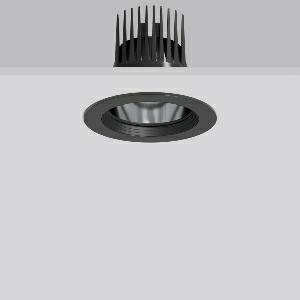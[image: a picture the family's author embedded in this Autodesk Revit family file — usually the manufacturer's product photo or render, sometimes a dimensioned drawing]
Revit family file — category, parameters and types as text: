
# Revit family: heledon_maxi_e_901765_003_2_6d95
name_source: partatom
category: Lighting Fixtures
units: mm (PartAtom-declared; Revit-internal decimal feet)

## family parameters
Cut with Voids When Loaded = No
Host = Face
Light Source = No
Part Type = Normal
Room Calculation Point = No
Round Connector Dimension = Use Diameter
Shared = No

## types (1)
- HELEDON maxi E (1 x LED Modul 927, 4100 lm, 2700)
    Apparent Load = 35 VA
    Approval mark = CE
    CIE Flux Codes = 100 100 100 100 100
    Color Rendering = 92
    Color Temperature = 2700
    Default Elevation = 1800 mm
    Description = Series: HELEDON maxi
Round recessed downlight. Housing: die-cast aluminium, powder-coated. Black plastic ring and recessed LED to prevent glare from the side. Optical assembly with reflector made of MIRO-Silver with 98% total light reflection for outstanding efficiency - can be changed without tools. Best colour rendering index Ra>90. Suitable for Recessed ceiling mounting. Installation without tools thanks to spring fastening system. Including separate LED converter with connecting cable 600 mm.High quality converter without flickering and stroboscopic effect. Through-wiring box (5 pole) available as accessory. The following accessories can be mounted without use of tools: interchangeable lenses, decorative glasses, honeycomb louvre, clear and frosted diffusers, white interchangeable plastic ring. 
Colour: deep black, matt (RAL 9005)
Diameter: 162 mm
Height: 3 mm
Cut-out diameter: 152 mm
Recess height: 200 mm
Luminaire: recess height: 135 mm
Lamp: LED
Socket: without socket
Colour temperature: 2700K
Colour rendering index (CRI): 92
System power: 35 W
Rated luminous flux: 4100 lm
Luminous efficiency: 117 lm/W
Control gear: Regulated power supply
Protection class: II
Type of protection: IP 20
    Height = 0 mm  [stored 0 ft]
    Lamp = 1 x LED Modul 927
    Lamp Light Flux = 4100 lm
    Lamp count = 1
    Length = 162 mm
    Lifetime = 50000 h
    Luminous efficacy = 117 lm/W
    Manufacturer = RZB
    ModVariant = No
    Model = 901765.003.2
    Mounting Place = Ceiling
    Mounting Type = Recessed
    Number of Poles = 1
    OnlyDefault = Yes
    Power Factor = 1
    Product Name = HELEDON maxi E
    Product group = Recessed downlights
    ProductGroupID = 402
    Protection Class = Protection class II
    Protection Degree = IP 20
    RLX_Detail_Level = 1
    RLX_Emergency_Light_Flux = 0 lm
    RLX_Emergency_Type = 0
    RLX_Emergency_Type_DB = No
    RlxData = <blob elided: 120549 chars, md5=c41866dd>
    Socket = socket
    Standby Power = 0 W
    System Light Flux = 4100 lm
    System Power = 35 W
    Type Comments = Product without accessories
    Type Image = 901662.003.jpg
    URL = http://relux.com
    VarID = ---
    Voltage = 230 V
    Voltage Range = 220-240 V
    Weight = 0.00 kg
    Width = 0 mm  [stored 0 ft]

note: [stored X ft] marks values corroborated as IEEE doubles in the binary element streams (Revit-internal decimal feet)

## geometry (parser evidence)
native form markers: Blend x4, Sweep x10
no freeform markers — native parametric forms only
